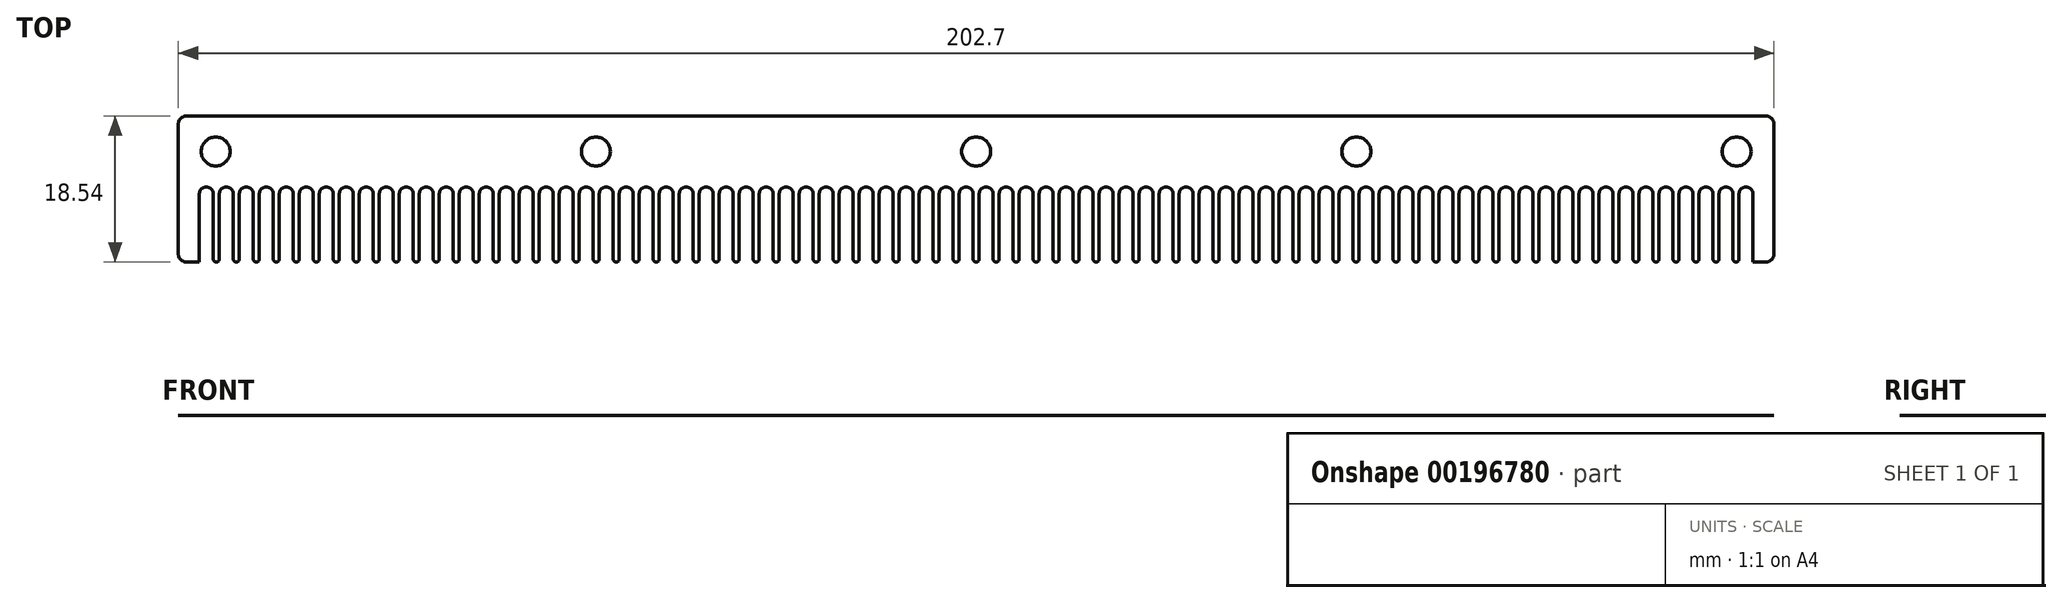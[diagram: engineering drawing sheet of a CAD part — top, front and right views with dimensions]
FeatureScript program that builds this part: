
annotation { "Feature Type Name" : "Feature", "Feature Type Description" : "" }
export const myFeature = defineFeature(function(context is Context, id is Id, definition is map)
    precondition{}
    {
        {
            var Q0;
            Q0=qCreatedBy(makeId("Top.planeOp"),FACE);
            var sketch = newSketch(context, id + "F0", { "sketchPlane" : qUnion([Q0])});
            skLineSegment(sketch, "E0.bottom", {"start": v(100.33, 9.52) * mm, "end": v(-100.33, 9.53) * mm});
            skLineSegment(sketch, "E0.left", {"start": v(101.6, 8.25) * mm, "end": v(101.6, -8.26) * mm});
            skLineSegment(sketch, "E0.right", {"start": v(-101.6, 8.26) * mm, "end": v(-101.6, -8.25) * mm});
            skPoint(sketch, "E0.middle", {"position": v(0, 0) * mm});
            skPoint(sketch, "E1.visualSharp", {"position": v(-101.6, 9.53) * mm});
            skArc(sketch, "E1.filletArc", {"start": v(-100.33, 9.53) * mm, "mid": v(-101.23, 9.15) * mm, "end": v(-101.6, 8.26) * mm});
            skPoint(sketch, "E2.visualSharp", {"position": v(-101.6, -9.52) * mm});
            skArc(sketch, "E2.filletArc", {"start": v(-101.6, -8.25) * mm, "mid": v(-101.23, -9.15) * mm, "end": v(-100.33, -9.52) * mm});
            skPoint(sketch, "E3.visualSharp", {"position": v(101.6, 9.52) * mm});
            skArc(sketch, "E3.filletArc", {"start": v(101.6, 8.25) * mm, "mid": v(101.23, 9.15) * mm, "end": v(100.33, 9.52) * mm});
            skPoint(sketch, "E4.visualSharp", {"position": v(101.6, -9.53) * mm});
            skArc(sketch, "E4.filletArc", {"start": v(100.33, -9.53) * mm, "mid": v(101.23, -9.15) * mm, "end": v(101.6, -8.26) * mm});
            skLineSegment(sketch, "E5", {"start": v(-98.42, -9.52) * mm, "end": v(-98.42, -0.63) * mm});
            skArc(sketch, "E6", {"start": v(-97.16, -0.63) * mm, "mid": v(-97.8, 0) * mm, "end": v(-98.43, -0.63) * mm});
            skLineSegment(sketch, "E7", {"start": v(-97.16, -0.63) * mm, "end": v(-97.16, -8.89) * mm});
            skArc(sketch, "E8", {"start": v(-97.16, -8.89) * mm, "mid": v(-96.52, -9.52) * mm, "end": v(-95.89, -8.89) * mm});
            skLineSegment(sketch, "E9", {"start": v(-95.89, -8.89) * mm, "end": v(-95.89, -0.63) * mm});
            skLineSegment(sketch, "E10.trimOffspring", {"start": v(-98.42, -9.52) * mm, "end": v(-100.33, -9.52) * mm});
            skArc(sketch, "E11.1.0.0", {"start": v(-94.62, -0.63) * mm, "mid": v(-95.25, 0) * mm, "end": v(-95.89, -0.63) * mm});
            skLineSegment(sketch, "E11.1.0.1", {"start": v(-94.62, -0.63) * mm, "end": v(-94.62, -8.89) * mm});
            skArc(sketch, "E11.1.0.2", {"start": v(-94.62, -8.89) * mm, "mid": v(-93.98, -9.52) * mm, "end": v(-93.35, -8.89) * mm});
            skLineSegment(sketch, "E11.1.0.3", {"start": v(-93.35, -8.89) * mm, "end": v(-93.35, -0.63) * mm});
            skArc(sketch, "E11.2.0.0", {"start": v(-92.08, -0.63) * mm, "mid": v(-92.71, 0) * mm, "end": v(-93.35, -0.63) * mm});
            skLineSegment(sketch, "E11.2.0.1", {"start": v(-92.08, -0.63) * mm, "end": v(-92.08, -8.89) * mm});
            skArc(sketch, "E11.2.0.2", {"start": v(-92.08, -8.89) * mm, "mid": v(-91.44, -9.52) * mm, "end": v(-90.8, -8.89) * mm});
            skLineSegment(sketch, "E11.2.0.3", {"start": v(-90.8, -8.89) * mm, "end": v(-90.8, -0.63) * mm});
            skArc(sketch, "E11.3.0.0", {"start": v(-89.54, -0.63) * mm, "mid": v(-90.17, 0) * mm, "end": v(-90.8, -0.63) * mm});
            skLineSegment(sketch, "E11.3.0.1", {"start": v(-89.54, -0.63) * mm, "end": v(-89.54, -8.89) * mm});
            skArc(sketch, "E11.3.0.2", {"start": v(-89.54, -8.89) * mm, "mid": v(-88.9, -9.52) * mm, "end": v(-88.27, -8.89) * mm});
            skLineSegment(sketch, "E11.3.0.3", {"start": v(-88.27, -8.89) * mm, "end": v(-88.27, -0.63) * mm});
            skArc(sketch, "E11.4.0.0", {"start": v(-87, -0.63) * mm, "mid": v(-87.63, 0) * mm, "end": v(-88.27, -0.63) * mm});
            skLineSegment(sketch, "E11.4.0.1", {"start": v(-87, -0.63) * mm, "end": v(-87, -8.89) * mm});
            skArc(sketch, "E11.4.0.2", {"start": v(-87, -8.89) * mm, "mid": v(-86.36, -9.52) * mm, "end": v(-85.73, -8.89) * mm});
            skLineSegment(sketch, "E11.4.0.3", {"start": v(-85.73, -8.89) * mm, "end": v(-85.73, -0.63) * mm});
            skArc(sketch, "E11.5.0.0", {"start": v(-84.46, -0.63) * mm, "mid": v(-85.1, 0) * mm, "end": v(-85.73, -0.63) * mm});
            skLineSegment(sketch, "E11.5.0.1", {"start": v(-84.46, -0.63) * mm, "end": v(-84.46, -8.89) * mm});
            skArc(sketch, "E11.5.0.2", {"start": v(-84.46, -8.89) * mm, "mid": v(-83.82, -9.52) * mm, "end": v(-83.19, -8.89) * mm});
            skLineSegment(sketch, "E11.5.0.3", {"start": v(-83.19, -8.89) * mm, "end": v(-83.19, -0.63) * mm});
            skArc(sketch, "E11.6.0.0", {"start": v(-81.92, -0.63) * mm, "mid": v(-82.55, 0) * mm, "end": v(-83.19, -0.63) * mm});
            skLineSegment(sketch, "E11.6.0.1", {"start": v(-81.92, -0.63) * mm, "end": v(-81.92, -8.89) * mm});
            skArc(sketch, "E11.6.0.2", {"start": v(-81.92, -8.89) * mm, "mid": v(-81.28, -9.52) * mm, "end": v(-80.65, -8.89) * mm});
            skLineSegment(sketch, "E11.6.0.3", {"start": v(-80.65, -8.89) * mm, "end": v(-80.65, -0.63) * mm});
            skArc(sketch, "E11.7.0.0", {"start": v(-79.38, -0.63) * mm, "mid": v(-80.01, 0) * mm, "end": v(-80.65, -0.63) * mm});
            skLineSegment(sketch, "E11.7.0.1", {"start": v(-79.38, -0.63) * mm, "end": v(-79.38, -8.89) * mm});
            skArc(sketch, "E11.7.0.2", {"start": v(-79.38, -8.89) * mm, "mid": v(-78.74, -9.52) * mm, "end": v(-78.1, -8.89) * mm});
            skLineSegment(sketch, "E11.7.0.3", {"start": v(-78.1, -8.89) * mm, "end": v(-78.1, -0.63) * mm});
            skArc(sketch, "E11.8.0.0", {"start": v(-76.84, -0.63) * mm, "mid": v(-77.47, 0) * mm, "end": v(-78.1, -0.63) * mm});
            skLineSegment(sketch, "E11.8.0.1", {"start": v(-76.84, -0.63) * mm, "end": v(-76.84, -8.89) * mm});
            skArc(sketch, "E11.8.0.2", {"start": v(-76.84, -8.89) * mm, "mid": v(-76.2, -9.52) * mm, "end": v(-75.57, -8.89) * mm});
            skLineSegment(sketch, "E11.8.0.3", {"start": v(-75.57, -8.89) * mm, "end": v(-75.57, -0.63) * mm});
            skArc(sketch, "E11.9.0.0", {"start": v(-74.3, -0.63) * mm, "mid": v(-74.93, 0) * mm, "end": v(-75.57, -0.63) * mm});
            skLineSegment(sketch, "E11.9.0.1", {"start": v(-74.3, -0.63) * mm, "end": v(-74.3, -8.89) * mm});
            skArc(sketch, "E11.9.0.2", {"start": v(-74.3, -8.89) * mm, "mid": v(-73.66, -9.52) * mm, "end": v(-73.03, -8.89) * mm});
            skLineSegment(sketch, "E11.9.0.3", {"start": v(-73.03, -8.89) * mm, "end": v(-73.03, -0.63) * mm});
            skArc(sketch, "E11.10.0.0", {"start": v(-71.76, -0.63) * mm, "mid": v(-72.4, 0) * mm, "end": v(-73.03, -0.63) * mm});
            skLineSegment(sketch, "E11.10.0.1", {"start": v(-71.76, -0.63) * mm, "end": v(-71.76, -8.89) * mm});
            skArc(sketch, "E11.10.0.2", {"start": v(-71.76, -8.89) * mm, "mid": v(-71.12, -9.52) * mm, "end": v(-70.49, -8.89) * mm});
            skLineSegment(sketch, "E11.10.0.3", {"start": v(-70.49, -8.89) * mm, "end": v(-70.49, -0.63) * mm});
            skArc(sketch, "E11.11.0.0", {"start": v(-69.22, -0.63) * mm, "mid": v(-69.85, 0) * mm, "end": v(-70.49, -0.63) * mm});
            skLineSegment(sketch, "E11.11.0.1", {"start": v(-69.22, -0.63) * mm, "end": v(-69.22, -8.89) * mm});
            skArc(sketch, "E11.11.0.2", {"start": v(-69.22, -8.89) * mm, "mid": v(-68.58, -9.52) * mm, "end": v(-67.95, -8.89) * mm});
            skLineSegment(sketch, "E11.11.0.3", {"start": v(-67.95, -8.89) * mm, "end": v(-67.95, -0.63) * mm});
            skArc(sketch, "E11.12.0.0", {"start": v(-66.68, -0.63) * mm, "mid": v(-67.31, 0) * mm, "end": v(-67.95, -0.63) * mm});
            skLineSegment(sketch, "E11.12.0.1", {"start": v(-66.68, -0.63) * mm, "end": v(-66.68, -8.89) * mm});
            skArc(sketch, "E11.12.0.2", {"start": v(-66.68, -8.89) * mm, "mid": v(-66.04, -9.52) * mm, "end": v(-65.4, -8.89) * mm});
            skLineSegment(sketch, "E11.12.0.3", {"start": v(-65.4, -8.89) * mm, "end": v(-65.4, -0.63) * mm});
            skArc(sketch, "E11.13.0.0", {"start": v(-64.14, -0.63) * mm, "mid": v(-64.77, 0) * mm, "end": v(-65.4, -0.63) * mm});
            skLineSegment(sketch, "E11.13.0.1", {"start": v(-64.14, -0.63) * mm, "end": v(-64.14, -8.89) * mm});
            skArc(sketch, "E11.13.0.2", {"start": v(-64.14, -8.89) * mm, "mid": v(-63.5, -9.52) * mm, "end": v(-62.87, -8.89) * mm});
            skLineSegment(sketch, "E11.13.0.3", {"start": v(-62.87, -8.89) * mm, "end": v(-62.87, -0.63) * mm});
            skArc(sketch, "E11.14.0.0", {"start": v(-61.6, -0.63) * mm, "mid": v(-62.23, 0) * mm, "end": v(-62.87, -0.63) * mm});
            skLineSegment(sketch, "E11.14.0.1", {"start": v(-61.6, -0.63) * mm, "end": v(-61.6, -8.89) * mm});
            skArc(sketch, "E11.14.0.2", {"start": v(-61.6, -8.89) * mm, "mid": v(-60.96, -9.52) * mm, "end": v(-60.33, -8.89) * mm});
            skLineSegment(sketch, "E11.14.0.3", {"start": v(-60.33, -8.89) * mm, "end": v(-60.33, -0.63) * mm});
            skArc(sketch, "E11.15.0.0", {"start": v(-59.06, -0.63) * mm, "mid": v(-59.7, 0) * mm, "end": v(-60.33, -0.63) * mm});
            skLineSegment(sketch, "E11.15.0.1", {"start": v(-59.06, -0.63) * mm, "end": v(-59.06, -8.89) * mm});
            skArc(sketch, "E11.15.0.2", {"start": v(-59.06, -8.89) * mm, "mid": v(-58.42, -9.52) * mm, "end": v(-57.79, -8.89) * mm});
            skLineSegment(sketch, "E11.15.0.3", {"start": v(-57.79, -8.89) * mm, "end": v(-57.79, -0.63) * mm});
            skArc(sketch, "E11.16.0.0", {"start": v(-56.52, -0.63) * mm, "mid": v(-57.15, 0) * mm, "end": v(-57.79, -0.63) * mm});
            skLineSegment(sketch, "E11.16.0.1", {"start": v(-56.52, -0.63) * mm, "end": v(-56.52, -8.89) * mm});
            skArc(sketch, "E11.16.0.2", {"start": v(-56.52, -8.89) * mm, "mid": v(-55.88, -9.52) * mm, "end": v(-55.25, -8.89) * mm});
            skLineSegment(sketch, "E11.16.0.3", {"start": v(-55.25, -8.89) * mm, "end": v(-55.25, -0.63) * mm});
            skArc(sketch, "E11.17.0.0", {"start": v(-53.98, -0.63) * mm, "mid": v(-54.61, 0) * mm, "end": v(-55.25, -0.63) * mm});
            skLineSegment(sketch, "E11.17.0.1", {"start": v(-53.98, -0.63) * mm, "end": v(-53.98, -8.89) * mm});
            skArc(sketch, "E11.17.0.2", {"start": v(-53.98, -8.89) * mm, "mid": v(-53.34, -9.52) * mm, "end": v(-52.7, -8.89) * mm});
            skLineSegment(sketch, "E11.17.0.3", {"start": v(-52.7, -8.89) * mm, "end": v(-52.7, -0.63) * mm});
            skArc(sketch, "E11.18.0.0", {"start": v(-51.44, -0.63) * mm, "mid": v(-52.07, 0) * mm, "end": v(-52.7, -0.63) * mm});
            skLineSegment(sketch, "E11.18.0.1", {"start": v(-51.44, -0.63) * mm, "end": v(-51.44, -8.89) * mm});
            skArc(sketch, "E11.18.0.2", {"start": v(-51.44, -8.89) * mm, "mid": v(-50.8, -9.52) * mm, "end": v(-50.17, -8.89) * mm});
            skLineSegment(sketch, "E11.18.0.3", {"start": v(-50.17, -8.89) * mm, "end": v(-50.17, -0.63) * mm});
            skArc(sketch, "E11.19.0.0", {"start": v(-48.9, -0.63) * mm, "mid": v(-49.53, 0) * mm, "end": v(-50.17, -0.63) * mm});
            skLineSegment(sketch, "E11.19.0.1", {"start": v(-48.9, -0.63) * mm, "end": v(-48.9, -8.89) * mm});
            skArc(sketch, "E11.19.0.2", {"start": v(-48.9, -8.89) * mm, "mid": v(-48.26, -9.52) * mm, "end": v(-47.63, -8.89) * mm});
            skLineSegment(sketch, "E11.19.0.3", {"start": v(-47.63, -8.89) * mm, "end": v(-47.63, -0.63) * mm});
            skArc(sketch, "E11.20.0.0", {"start": v(-46.36, -0.63) * mm, "mid": v(-47, 0) * mm, "end": v(-47.63, -0.63) * mm});
            skLineSegment(sketch, "E11.20.0.1", {"start": v(-46.36, -0.63) * mm, "end": v(-46.36, -8.89) * mm});
            skArc(sketch, "E11.20.0.2", {"start": v(-46.36, -8.89) * mm, "mid": v(-45.72, -9.52) * mm, "end": v(-45.09, -8.89) * mm});
            skLineSegment(sketch, "E11.20.0.3", {"start": v(-45.09, -8.89) * mm, "end": v(-45.09, -0.63) * mm});
            skArc(sketch, "E11.21.0.0", {"start": v(-43.82, -0.63) * mm, "mid": v(-44.45, 0) * mm, "end": v(-45.09, -0.63) * mm});
            skLineSegment(sketch, "E11.21.0.1", {"start": v(-43.82, -0.63) * mm, "end": v(-43.82, -8.89) * mm});
            skArc(sketch, "E11.21.0.2", {"start": v(-43.82, -8.89) * mm, "mid": v(-43.18, -9.52) * mm, "end": v(-42.55, -8.89) * mm});
            skLineSegment(sketch, "E11.21.0.3", {"start": v(-42.55, -8.89) * mm, "end": v(-42.55, -0.63) * mm});
            skArc(sketch, "E11.22.0.0", {"start": v(-41.28, -0.63) * mm, "mid": v(-41.91, 0) * mm, "end": v(-42.55, -0.63) * mm});
            skLineSegment(sketch, "E11.22.0.1", {"start": v(-41.28, -0.63) * mm, "end": v(-41.28, -8.89) * mm});
            skArc(sketch, "E11.22.0.2", {"start": v(-41.28, -8.89) * mm, "mid": v(-40.64, -9.52) * mm, "end": v(-40, -8.89) * mm});
            skLineSegment(sketch, "E11.22.0.3", {"start": v(-40, -8.89) * mm, "end": v(-40, -0.63) * mm});
            skArc(sketch, "E11.23.0.0", {"start": v(-38.74, -0.63) * mm, "mid": v(-39.37, 0) * mm, "end": v(-40, -0.63) * mm});
            skLineSegment(sketch, "E11.23.0.1", {"start": v(-38.74, -0.63) * mm, "end": v(-38.74, -8.89) * mm});
            skArc(sketch, "E11.23.0.2", {"start": v(-38.74, -8.89) * mm, "mid": v(-38.1, -9.52) * mm, "end": v(-37.47, -8.89) * mm});
            skLineSegment(sketch, "E11.23.0.3", {"start": v(-37.47, -8.89) * mm, "end": v(-37.47, -0.63) * mm});
            skArc(sketch, "E11.24.0.0", {"start": v(-36.2, -0.63) * mm, "mid": v(-36.83, 0) * mm, "end": v(-37.47, -0.63) * mm});
            skLineSegment(sketch, "E11.24.0.1", {"start": v(-36.2, -0.63) * mm, "end": v(-36.2, -8.89) * mm});
            skArc(sketch, "E11.24.0.2", {"start": v(-36.2, -8.89) * mm, "mid": v(-35.56, -9.52) * mm, "end": v(-34.93, -8.89) * mm});
            skLineSegment(sketch, "E11.24.0.3", {"start": v(-34.93, -8.89) * mm, "end": v(-34.93, -0.63) * mm});
            skArc(sketch, "E11.25.0.0", {"start": v(-33.66, -0.63) * mm, "mid": v(-34.3, 0) * mm, "end": v(-34.93, -0.63) * mm});
            skLineSegment(sketch, "E11.25.0.1", {"start": v(-33.66, -0.63) * mm, "end": v(-33.66, -8.89) * mm});
            skArc(sketch, "E11.25.0.2", {"start": v(-33.66, -8.89) * mm, "mid": v(-33.02, -9.52) * mm, "end": v(-32.39, -8.89) * mm});
            skLineSegment(sketch, "E11.25.0.3", {"start": v(-32.39, -8.89) * mm, "end": v(-32.39, -0.63) * mm});
            skArc(sketch, "E11.26.0.0", {"start": v(-31.12, -0.63) * mm, "mid": v(-31.75, 0) * mm, "end": v(-32.39, -0.63) * mm});
            skLineSegment(sketch, "E11.26.0.1", {"start": v(-31.12, -0.63) * mm, "end": v(-31.12, -8.89) * mm});
            skArc(sketch, "E11.26.0.2", {"start": v(-31.12, -8.89) * mm, "mid": v(-30.48, -9.52) * mm, "end": v(-29.85, -8.89) * mm});
            skLineSegment(sketch, "E11.26.0.3", {"start": v(-29.85, -8.89) * mm, "end": v(-29.85, -0.63) * mm});
            skArc(sketch, "E11.27.0.0", {"start": v(-28.58, -0.63) * mm, "mid": v(-29.21, 0) * mm, "end": v(-29.85, -0.63) * mm});
            skLineSegment(sketch, "E11.27.0.1", {"start": v(-28.58, -0.63) * mm, "end": v(-28.58, -8.89) * mm});
            skArc(sketch, "E11.27.0.2", {"start": v(-28.58, -8.89) * mm, "mid": v(-27.94, -9.52) * mm, "end": v(-27.3, -8.89) * mm});
            skLineSegment(sketch, "E11.27.0.3", {"start": v(-27.3, -8.89) * mm, "end": v(-27.3, -0.63) * mm});
            skArc(sketch, "E11.28.0.0", {"start": v(-26.04, -0.63) * mm, "mid": v(-26.67, 0) * mm, "end": v(-27.3, -0.63) * mm});
            skLineSegment(sketch, "E11.28.0.1", {"start": v(-26.04, -0.63) * mm, "end": v(-26.04, -8.89) * mm});
            skArc(sketch, "E11.28.0.2", {"start": v(-26.04, -8.89) * mm, "mid": v(-25.4, -9.52) * mm, "end": v(-24.77, -8.89) * mm});
            skLineSegment(sketch, "E11.28.0.3", {"start": v(-24.77, -8.89) * mm, "end": v(-24.77, -0.63) * mm});
            skArc(sketch, "E11.29.0.0", {"start": v(-23.5, -0.63) * mm, "mid": v(-24.13, 0) * mm, "end": v(-24.77, -0.63) * mm});
            skLineSegment(sketch, "E11.29.0.1", {"start": v(-23.5, -0.63) * mm, "end": v(-23.5, -8.89) * mm});
            skArc(sketch, "E11.29.0.2", {"start": v(-23.5, -8.89) * mm, "mid": v(-22.86, -9.52) * mm, "end": v(-22.23, -8.89) * mm});
            skLineSegment(sketch, "E11.29.0.3", {"start": v(-22.23, -8.89) * mm, "end": v(-22.23, -0.63) * mm});
            skArc(sketch, "E11.30.0.0", {"start": v(-20.96, -0.63) * mm, "mid": v(-21.6, 0) * mm, "end": v(-22.23, -0.63) * mm});
            skLineSegment(sketch, "E11.30.0.1", {"start": v(-20.96, -0.63) * mm, "end": v(-20.96, -8.89) * mm});
            skArc(sketch, "E11.30.0.2", {"start": v(-20.96, -8.89) * mm, "mid": v(-20.32, -9.52) * mm, "end": v(-19.69, -8.89) * mm});
            skLineSegment(sketch, "E11.30.0.3", {"start": v(-19.69, -8.89) * mm, "end": v(-19.69, -0.63) * mm});
            skArc(sketch, "E11.31.0.0", {"start": v(-18.42, -0.63) * mm, "mid": v(-19.05, 0) * mm, "end": v(-19.69, -0.63) * mm});
            skLineSegment(sketch, "E11.31.0.1", {"start": v(-18.41, -0.63) * mm, "end": v(-18.41, -8.89) * mm});
            skArc(sketch, "E11.31.0.2", {"start": v(-18.41, -8.89) * mm, "mid": v(-17.78, -9.52) * mm, "end": v(-17.15, -8.89) * mm});
            skLineSegment(sketch, "E11.31.0.3", {"start": v(-17.15, -8.89) * mm, "end": v(-17.15, -0.63) * mm});
            skArc(sketch, "E11.32.0.0", {"start": v(-15.88, -0.63) * mm, "mid": v(-16.51, 0) * mm, "end": v(-17.15, -0.63) * mm});
            skLineSegment(sketch, "E11.32.0.1", {"start": v(-15.88, -0.63) * mm, "end": v(-15.88, -8.89) * mm});
            skArc(sketch, "E11.32.0.2", {"start": v(-15.88, -8.89) * mm, "mid": v(-15.24, -9.52) * mm, "end": v(-14.6, -8.89) * mm});
            skLineSegment(sketch, "E11.32.0.3", {"start": v(-14.6, -8.89) * mm, "end": v(-14.6, -0.63) * mm});
            skArc(sketch, "E11.33.0.0", {"start": v(-13.34, -0.63) * mm, "mid": v(-13.97, 0) * mm, "end": v(-14.6, -0.63) * mm});
            skLineSegment(sketch, "E11.33.0.1", {"start": v(-13.33, -0.63) * mm, "end": v(-13.33, -8.89) * mm});
            skArc(sketch, "E11.33.0.2", {"start": v(-13.33, -8.89) * mm, "mid": v(-12.7, -9.52) * mm, "end": v(-12.07, -8.89) * mm});
            skLineSegment(sketch, "E11.33.0.3", {"start": v(-12.07, -8.89) * mm, "end": v(-12.07, -0.63) * mm});
            skArc(sketch, "E11.34.0.0", {"start": v(-10.8, -0.63) * mm, "mid": v(-11.43, 0) * mm, "end": v(-12.07, -0.63) * mm});
            skLineSegment(sketch, "E11.34.0.1", {"start": v(-10.8, -0.63) * mm, "end": v(-10.8, -8.89) * mm});
            skArc(sketch, "E11.34.0.2", {"start": v(-10.8, -8.89) * mm, "mid": v(-10.16, -9.52) * mm, "end": v(-9.53, -8.89) * mm});
            skLineSegment(sketch, "E11.34.0.3", {"start": v(-9.53, -8.89) * mm, "end": v(-9.53, -0.63) * mm});
            skArc(sketch, "E11.35.0.0", {"start": v(-8.26, -0.63) * mm, "mid": v(-8.9, 0) * mm, "end": v(-9.53, -0.63) * mm});
            skLineSegment(sketch, "E11.35.0.1", {"start": v(-8.25, -0.63) * mm, "end": v(-8.25, -8.89) * mm});
            skArc(sketch, "E11.35.0.2", {"start": v(-8.25, -8.89) * mm, "mid": v(-7.62, -9.52) * mm, "end": v(-6.99, -8.89) * mm});
            skLineSegment(sketch, "E11.35.0.3", {"start": v(-6.99, -8.89) * mm, "end": v(-6.99, -0.63) * mm});
            skArc(sketch, "E11.36.0.0", {"start": v(-5.72, -0.63) * mm, "mid": v(-6.35, 0) * mm, "end": v(-6.99, -0.63) * mm});
            skLineSegment(sketch, "E11.36.0.1", {"start": v(-5.71, -0.63) * mm, "end": v(-5.71, -8.89) * mm});
            skArc(sketch, "E11.36.0.2", {"start": v(-5.71, -8.89) * mm, "mid": v(-5.08, -9.52) * mm, "end": v(-4.45, -8.89) * mm});
            skLineSegment(sketch, "E11.36.0.3", {"start": v(-4.45, -8.89) * mm, "end": v(-4.45, -0.63) * mm});
            skArc(sketch, "E11.37.0.0", {"start": v(-3.18, -0.63) * mm, "mid": v(-3.81, 0) * mm, "end": v(-4.45, -0.63) * mm});
            skLineSegment(sketch, "E11.37.0.1", {"start": v(-3.17, -0.63) * mm, "end": v(-3.17, -8.89) * mm});
            skArc(sketch, "E11.37.0.2", {"start": v(-3.17, -8.89) * mm, "mid": v(-2.54, -9.52) * mm, "end": v(-1.9, -8.89) * mm});
            skLineSegment(sketch, "E11.37.0.3", {"start": v(-1.9, -8.89) * mm, "end": v(-1.9, -0.63) * mm});
            skArc(sketch, "E11.38.0.0", {"start": v(-0.64, -0.63) * mm, "mid": v(-1.27, 0) * mm, "end": v(-1.9, -0.63) * mm});
            skLineSegment(sketch, "E11.38.0.1", {"start": v(-0.63, -0.63) * mm, "end": v(-0.63, -8.89) * mm});
            skArc(sketch, "E11.38.0.2", {"start": v(-0.63, -8.89) * mm, "mid": v(0, -9.52) * mm, "end": v(0.63, -8.89) * mm});
            skLineSegment(sketch, "E11.38.0.3", {"start": v(0.63, -8.89) * mm, "end": v(0.63, -0.63) * mm});
            skArc(sketch, "E11.39.0.0", {"start": v(1.9, -0.63) * mm, "mid": v(1.27, 0) * mm, "end": v(0.63, -0.63) * mm});
            skLineSegment(sketch, "E11.39.0.1", {"start": v(1.9, -0.63) * mm, "end": v(1.9, -8.89) * mm});
            skArc(sketch, "E11.39.0.2", {"start": v(1.9, -8.89) * mm, "mid": v(2.54, -9.52) * mm, "end": v(3.17, -8.89) * mm});
            skLineSegment(sketch, "E11.39.0.3", {"start": v(3.17, -8.89) * mm, "end": v(3.17, -0.63) * mm});
            skArc(sketch, "E11.40.0.0", {"start": v(4.44, -0.63) * mm, "mid": v(3.8, 0) * mm, "end": v(3.17, -0.63) * mm});
            skLineSegment(sketch, "E11.40.0.1", {"start": v(4.45, -0.63) * mm, "end": v(4.45, -8.89) * mm});
            skArc(sketch, "E11.40.0.2", {"start": v(4.45, -8.89) * mm, "mid": v(5.08, -9.52) * mm, "end": v(5.71, -8.89) * mm});
            skLineSegment(sketch, "E11.40.0.3", {"start": v(5.71, -8.89) * mm, "end": v(5.71, -0.63) * mm});
            skArc(sketch, "E11.41.0.0", {"start": v(6.98, -0.63) * mm, "mid": v(6.35, 0) * mm, "end": v(5.71, -0.63) * mm});
            skLineSegment(sketch, "E11.41.0.1", {"start": v(6.99, -0.63) * mm, "end": v(6.99, -8.89) * mm});
            skArc(sketch, "E11.41.0.2", {"start": v(6.99, -8.89) * mm, "mid": v(7.62, -9.52) * mm, "end": v(8.25, -8.89) * mm});
            skLineSegment(sketch, "E11.41.0.3", {"start": v(8.25, -8.89) * mm, "end": v(8.25, -0.63) * mm});
            skArc(sketch, "E11.42.0.0", {"start": v(9.52, -0.63) * mm, "mid": v(8.9, 0) * mm, "end": v(8.25, -0.63) * mm});
            skLineSegment(sketch, "E11.42.0.1", {"start": v(9.53, -0.63) * mm, "end": v(9.53, -8.89) * mm});
            skArc(sketch, "E11.42.0.2", {"start": v(9.53, -8.89) * mm, "mid": v(10.16, -9.52) * mm, "end": v(10.8, -8.89) * mm});
            skLineSegment(sketch, "E11.42.0.3", {"start": v(10.8, -8.89) * mm, "end": v(10.8, -0.63) * mm});
            skArc(sketch, "E11.43.0.0", {"start": v(12.06, -0.63) * mm, "mid": v(11.43, 0) * mm, "end": v(10.8, -0.63) * mm});
            skLineSegment(sketch, "E11.43.0.1", {"start": v(12.07, -0.63) * mm, "end": v(12.07, -8.89) * mm});
            skArc(sketch, "E11.43.0.2", {"start": v(12.07, -8.89) * mm, "mid": v(12.7, -9.52) * mm, "end": v(13.33, -8.89) * mm});
            skLineSegment(sketch, "E11.43.0.3", {"start": v(13.33, -8.89) * mm, "end": v(13.33, -0.63) * mm});
            skArc(sketch, "E11.44.0.0", {"start": v(14.6, -0.63) * mm, "mid": v(13.97, 0) * mm, "end": v(13.33, -0.63) * mm});
            skLineSegment(sketch, "E11.44.0.1", {"start": v(14.6, -0.63) * mm, "end": v(14.6, -8.89) * mm});
            skArc(sketch, "E11.44.0.2", {"start": v(14.6, -8.89) * mm, "mid": v(15.24, -9.52) * mm, "end": v(15.88, -8.89) * mm});
            skLineSegment(sketch, "E11.44.0.3", {"start": v(15.88, -8.89) * mm, "end": v(15.88, -0.63) * mm});
            skArc(sketch, "E11.45.0.0", {"start": v(17.14, -0.63) * mm, "mid": v(16.51, 0) * mm, "end": v(15.88, -0.63) * mm});
            skLineSegment(sketch, "E11.45.0.1", {"start": v(17.15, -0.63) * mm, "end": v(17.15, -8.89) * mm});
            skArc(sketch, "E11.45.0.2", {"start": v(17.15, -8.89) * mm, "mid": v(17.78, -9.52) * mm, "end": v(18.41, -8.89) * mm});
            skLineSegment(sketch, "E11.45.0.3", {"start": v(18.41, -8.89) * mm, "end": v(18.41, -0.63) * mm});
            skArc(sketch, "E11.46.0.0", {"start": v(19.68, -0.63) * mm, "mid": v(19.05, 0) * mm, "end": v(18.41, -0.63) * mm});
            skLineSegment(sketch, "E11.46.0.1", {"start": v(19.69, -0.63) * mm, "end": v(19.69, -8.89) * mm});
            skArc(sketch, "E11.46.0.2", {"start": v(19.69, -8.89) * mm, "mid": v(20.32, -9.52) * mm, "end": v(20.96, -8.89) * mm});
            skLineSegment(sketch, "E11.46.0.3", {"start": v(20.96, -8.89) * mm, "end": v(20.96, -0.63) * mm});
            skArc(sketch, "E11.47.0.0", {"start": v(22.22, -0.63) * mm, "mid": v(21.59, 0) * mm, "end": v(20.96, -0.63) * mm});
            skLineSegment(sketch, "E11.47.0.1", {"start": v(22.23, -0.63) * mm, "end": v(22.23, -8.89) * mm});
            skArc(sketch, "E11.47.0.2", {"start": v(22.23, -8.89) * mm, "mid": v(22.86, -9.52) * mm, "end": v(23.5, -8.89) * mm});
            skLineSegment(sketch, "E11.47.0.3", {"start": v(23.5, -8.89) * mm, "end": v(23.5, -0.63) * mm});
            skArc(sketch, "E11.48.0.0", {"start": v(24.76, -0.63) * mm, "mid": v(24.13, 0) * mm, "end": v(23.5, -0.63) * mm});
            skLineSegment(sketch, "E11.48.0.1", {"start": v(24.77, -0.63) * mm, "end": v(24.77, -8.89) * mm});
            skArc(sketch, "E11.48.0.2", {"start": v(24.77, -8.89) * mm, "mid": v(25.4, -9.52) * mm, "end": v(26.04, -8.89) * mm});
            skLineSegment(sketch, "E11.48.0.3", {"start": v(26.04, -8.89) * mm, "end": v(26.04, -0.63) * mm});
            skArc(sketch, "E11.49.0.0", {"start": v(27.3, -0.63) * mm, "mid": v(26.67, 0) * mm, "end": v(26.04, -0.63) * mm});
            skLineSegment(sketch, "E11.49.0.1", {"start": v(27.3, -0.63) * mm, "end": v(27.3, -8.89) * mm});
            skArc(sketch, "E11.49.0.2", {"start": v(27.3, -8.89) * mm, "mid": v(27.94, -9.52) * mm, "end": v(28.58, -8.89) * mm});
            skLineSegment(sketch, "E11.49.0.3", {"start": v(28.58, -8.89) * mm, "end": v(28.58, -0.63) * mm});
            skArc(sketch, "E11.50.0.0", {"start": v(29.84, -0.63) * mm, "mid": v(29.21, 0) * mm, "end": v(28.58, -0.63) * mm});
            skLineSegment(sketch, "E11.50.0.1", {"start": v(29.85, -0.63) * mm, "end": v(29.85, -8.89) * mm});
            skArc(sketch, "E11.50.0.2", {"start": v(29.85, -8.89) * mm, "mid": v(30.48, -9.52) * mm, "end": v(31.12, -8.89) * mm});
            skLineSegment(sketch, "E11.50.0.3", {"start": v(31.12, -8.89) * mm, "end": v(31.12, -0.63) * mm});
            skArc(sketch, "E11.51.0.0", {"start": v(32.39, -0.63) * mm, "mid": v(31.75, 0) * mm, "end": v(31.12, -0.63) * mm});
            skLineSegment(sketch, "E11.51.0.1", {"start": v(32.39, -0.63) * mm, "end": v(32.39, -8.89) * mm});
            skArc(sketch, "E11.51.0.2", {"start": v(32.39, -8.89) * mm, "mid": v(33.02, -9.52) * mm, "end": v(33.66, -8.89) * mm});
            skLineSegment(sketch, "E11.51.0.3", {"start": v(33.66, -8.89) * mm, "end": v(33.66, -0.63) * mm});
            skArc(sketch, "E11.52.0.0", {"start": v(34.92, -0.63) * mm, "mid": v(34.3, 0) * mm, "end": v(33.66, -0.63) * mm});
            skLineSegment(sketch, "E11.52.0.1", {"start": v(34.93, -0.63) * mm, "end": v(34.93, -8.89) * mm});
            skArc(sketch, "E11.52.0.2", {"start": v(34.93, -8.89) * mm, "mid": v(35.56, -9.52) * mm, "end": v(36.2, -8.89) * mm});
            skLineSegment(sketch, "E11.52.0.3", {"start": v(36.2, -8.89) * mm, "end": v(36.2, -0.63) * mm});
            skArc(sketch, "E11.53.0.0", {"start": v(37.46, -0.63) * mm, "mid": v(36.83, 0) * mm, "end": v(36.2, -0.63) * mm});
            skLineSegment(sketch, "E11.53.0.1", {"start": v(37.46, -0.63) * mm, "end": v(37.46, -8.89) * mm});
            skArc(sketch, "E11.53.0.2", {"start": v(37.46, -8.89) * mm, "mid": v(38.1, -9.52) * mm, "end": v(38.73, -8.89) * mm});
            skLineSegment(sketch, "E11.53.0.3", {"start": v(38.73, -8.89) * mm, "end": v(38.73, -0.63) * mm});
            skArc(sketch, "E11.54.0.0", {"start": v(40, -0.63) * mm, "mid": v(39.37, 0) * mm, "end": v(38.74, -0.63) * mm});
            skLineSegment(sketch, "E11.54.0.1", {"start": v(40, -0.63) * mm, "end": v(40, -8.89) * mm});
            skArc(sketch, "E11.54.0.2", {"start": v(40, -8.89) * mm, "mid": v(40.64, -9.52) * mm, "end": v(41.28, -8.89) * mm});
            skLineSegment(sketch, "E11.54.0.3", {"start": v(41.28, -8.89) * mm, "end": v(41.28, -0.63) * mm});
            skArc(sketch, "E11.55.0.0", {"start": v(42.55, -0.63) * mm, "mid": v(41.91, 0) * mm, "end": v(41.28, -0.63) * mm});
            skLineSegment(sketch, "E11.55.0.1", {"start": v(42.55, -0.63) * mm, "end": v(42.55, -8.89) * mm});
            skArc(sketch, "E11.55.0.2", {"start": v(42.55, -8.89) * mm, "mid": v(43.18, -9.52) * mm, "end": v(43.82, -8.89) * mm});
            skLineSegment(sketch, "E11.55.0.3", {"start": v(43.82, -8.89) * mm, "end": v(43.82, -0.63) * mm});
            skArc(sketch, "E11.56.0.0", {"start": v(45.09, -0.63) * mm, "mid": v(44.45, 0) * mm, "end": v(43.82, -0.63) * mm});
            skLineSegment(sketch, "E11.56.0.1", {"start": v(45.09, -0.63) * mm, "end": v(45.09, -8.89) * mm});
            skArc(sketch, "E11.56.0.2", {"start": v(45.09, -8.89) * mm, "mid": v(45.72, -9.52) * mm, "end": v(46.36, -8.89) * mm});
            skLineSegment(sketch, "E11.56.0.3", {"start": v(46.36, -8.89) * mm, "end": v(46.36, -0.63) * mm});
            skArc(sketch, "E11.57.0.0", {"start": v(47.62, -0.63) * mm, "mid": v(46.99, 0) * mm, "end": v(46.35, -0.63) * mm});
            skLineSegment(sketch, "E11.57.0.1", {"start": v(47.62, -0.63) * mm, "end": v(47.62, -8.89) * mm});
            skArc(sketch, "E11.57.0.2", {"start": v(47.62, -8.89) * mm, "mid": v(48.26, -9.52) * mm, "end": v(48.9, -8.89) * mm});
            skLineSegment(sketch, "E11.57.0.3", {"start": v(48.9, -8.89) * mm, "end": v(48.9, -0.63) * mm});
            skArc(sketch, "E11.58.0.0", {"start": v(50.16, -0.63) * mm, "mid": v(49.53, 0) * mm, "end": v(48.9, -0.63) * mm});
            skLineSegment(sketch, "E11.58.0.1", {"start": v(50.17, -0.63) * mm, "end": v(50.17, -8.89) * mm});
            skArc(sketch, "E11.58.0.2", {"start": v(50.17, -8.89) * mm, "mid": v(50.8, -9.52) * mm, "end": v(51.44, -8.89) * mm});
            skLineSegment(sketch, "E11.58.0.3", {"start": v(51.44, -8.89) * mm, "end": v(51.44, -0.63) * mm});
            skArc(sketch, "E11.59.0.0", {"start": v(52.7, -0.63) * mm, "mid": v(52.07, 0) * mm, "end": v(51.44, -0.63) * mm});
            skLineSegment(sketch, "E11.59.0.1", {"start": v(52.7, -0.63) * mm, "end": v(52.7, -8.89) * mm});
            skArc(sketch, "E11.59.0.2", {"start": v(52.7, -8.89) * mm, "mid": v(53.34, -9.52) * mm, "end": v(53.98, -8.89) * mm});
            skLineSegment(sketch, "E11.59.0.3", {"start": v(53.98, -8.89) * mm, "end": v(53.98, -0.63) * mm});
            skArc(sketch, "E11.60.0.0", {"start": v(55.25, -0.63) * mm, "mid": v(54.61, 0) * mm, "end": v(53.98, -0.63) * mm});
            skLineSegment(sketch, "E11.60.0.1", {"start": v(55.25, -0.63) * mm, "end": v(55.25, -8.89) * mm});
            skArc(sketch, "E11.60.0.2", {"start": v(55.25, -8.89) * mm, "mid": v(55.88, -9.52) * mm, "end": v(56.52, -8.89) * mm});
            skLineSegment(sketch, "E11.60.0.3", {"start": v(56.52, -8.89) * mm, "end": v(56.52, -0.63) * mm});
            skArc(sketch, "E11.61.0.0", {"start": v(57.78, -0.63) * mm, "mid": v(57.15, 0) * mm, "end": v(56.51, -0.63) * mm});
            skLineSegment(sketch, "E11.61.0.1", {"start": v(57.79, -0.63) * mm, "end": v(57.79, -8.89) * mm});
            skArc(sketch, "E11.61.0.2", {"start": v(57.79, -8.89) * mm, "mid": v(58.42, -9.52) * mm, "end": v(59.05, -8.89) * mm});
            skLineSegment(sketch, "E11.61.0.3", {"start": v(59.05, -8.89) * mm, "end": v(59.05, -0.63) * mm});
            skArc(sketch, "E11.62.0.0", {"start": v(60.33, -0.63) * mm, "mid": v(59.7, 0) * mm, "end": v(59.06, -0.63) * mm});
            skLineSegment(sketch, "E11.62.0.1", {"start": v(60.33, -0.63) * mm, "end": v(60.33, -8.89) * mm});
            skArc(sketch, "E11.62.0.2", {"start": v(60.33, -8.89) * mm, "mid": v(60.96, -9.52) * mm, "end": v(61.6, -8.89) * mm});
            skLineSegment(sketch, "E11.62.0.3", {"start": v(61.6, -8.89) * mm, "end": v(61.6, -0.63) * mm});
            skArc(sketch, "E11.63.0.0", {"start": v(62.87, -0.63) * mm, "mid": v(62.23, 0) * mm, "end": v(61.6, -0.63) * mm});
            skLineSegment(sketch, "E11.63.0.1", {"start": v(62.87, -0.63) * mm, "end": v(62.87, -8.89) * mm});
            skArc(sketch, "E11.63.0.2", {"start": v(62.87, -8.89) * mm, "mid": v(63.5, -9.52) * mm, "end": v(64.14, -8.89) * mm});
            skLineSegment(sketch, "E11.63.0.3", {"start": v(64.14, -8.89) * mm, "end": v(64.14, -0.63) * mm});
            skArc(sketch, "E11.64.0.0", {"start": v(65.4, -0.63) * mm, "mid": v(64.77, 0) * mm, "end": v(64.14, -0.63) * mm});
            skLineSegment(sketch, "E11.64.0.1", {"start": v(65.4, -0.63) * mm, "end": v(65.4, -8.89) * mm});
            skArc(sketch, "E11.64.0.2", {"start": v(65.4, -8.89) * mm, "mid": v(66.04, -9.52) * mm, "end": v(66.68, -8.89) * mm});
            skLineSegment(sketch, "E11.64.0.3", {"start": v(66.68, -8.89) * mm, "end": v(66.68, -0.63) * mm});
            skArc(sketch, "E11.65.0.0", {"start": v(67.94, -0.63) * mm, "mid": v(67.3, 0) * mm, "end": v(66.67, -0.63) * mm});
            skLineSegment(sketch, "E11.65.0.1", {"start": v(67.95, -0.63) * mm, "end": v(67.95, -8.89) * mm});
            skArc(sketch, "E11.65.0.2", {"start": v(67.95, -8.89) * mm, "mid": v(68.58, -9.52) * mm, "end": v(69.22, -8.89) * mm});
            skLineSegment(sketch, "E11.65.0.3", {"start": v(69.22, -8.89) * mm, "end": v(69.22, -0.63) * mm});
            skArc(sketch, "E11.66.0.0", {"start": v(70.48, -0.63) * mm, "mid": v(69.85, 0) * mm, "end": v(69.22, -0.63) * mm});
            skLineSegment(sketch, "E11.66.0.1", {"start": v(70.49, -0.63) * mm, "end": v(70.49, -8.89) * mm});
            skArc(sketch, "E11.66.0.2", {"start": v(70.49, -8.89) * mm, "mid": v(71.12, -9.52) * mm, "end": v(71.76, -8.89) * mm});
            skLineSegment(sketch, "E11.66.0.3", {"start": v(71.76, -8.89) * mm, "end": v(71.76, -0.63) * mm});
            skArc(sketch, "E11.67.0.0", {"start": v(73.03, -0.63) * mm, "mid": v(72.4, 0) * mm, "end": v(71.76, -0.63) * mm});
            skLineSegment(sketch, "E11.67.0.1", {"start": v(73.03, -0.63) * mm, "end": v(73.03, -8.89) * mm});
            skArc(sketch, "E11.67.0.2", {"start": v(73.03, -8.89) * mm, "mid": v(73.66, -9.52) * mm, "end": v(74.3, -8.89) * mm});
            skLineSegment(sketch, "E11.67.0.3", {"start": v(74.3, -8.89) * mm, "end": v(74.3, -0.63) * mm});
            skArc(sketch, "E11.68.0.0", {"start": v(75.57, -0.63) * mm, "mid": v(74.93, 0) * mm, "end": v(74.3, -0.63) * mm});
            skLineSegment(sketch, "E11.68.0.1", {"start": v(75.57, -0.63) * mm, "end": v(75.57, -8.89) * mm});
            skArc(sketch, "E11.68.0.2", {"start": v(75.57, -8.89) * mm, "mid": v(76.2, -9.52) * mm, "end": v(76.84, -8.89) * mm});
            skLineSegment(sketch, "E11.68.0.3", {"start": v(76.84, -8.89) * mm, "end": v(76.84, -0.63) * mm});
            skArc(sketch, "E11.69.0.0", {"start": v(78.1, -0.63) * mm, "mid": v(77.47, 0) * mm, "end": v(76.83, -0.63) * mm});
            skLineSegment(sketch, "E11.69.0.1", {"start": v(78.1, -0.63) * mm, "end": v(78.1, -8.89) * mm});
            skArc(sketch, "E11.69.0.2", {"start": v(78.1, -8.89) * mm, "mid": v(78.74, -9.52) * mm, "end": v(79.38, -8.89) * mm});
            skLineSegment(sketch, "E11.69.0.3", {"start": v(79.38, -8.89) * mm, "end": v(79.38, -0.63) * mm});
            skArc(sketch, "E11.70.0.0", {"start": v(80.65, -0.63) * mm, "mid": v(80.01, 0) * mm, "end": v(79.38, -0.63) * mm});
            skLineSegment(sketch, "E11.70.0.1", {"start": v(80.65, -0.63) * mm, "end": v(80.65, -8.89) * mm});
            skArc(sketch, "E11.70.0.2", {"start": v(80.65, -8.89) * mm, "mid": v(81.28, -9.52) * mm, "end": v(81.92, -8.89) * mm});
            skLineSegment(sketch, "E11.70.0.3", {"start": v(81.92, -8.89) * mm, "end": v(81.92, -0.63) * mm});
            skArc(sketch, "E11.71.0.0", {"start": v(83.19, -0.63) * mm, "mid": v(82.55, 0) * mm, "end": v(81.92, -0.63) * mm});
            skLineSegment(sketch, "E11.71.0.1", {"start": v(83.19, -0.63) * mm, "end": v(83.19, -8.89) * mm});
            skArc(sketch, "E11.71.0.2", {"start": v(83.19, -8.89) * mm, "mid": v(83.82, -9.52) * mm, "end": v(84.46, -8.89) * mm});
            skLineSegment(sketch, "E11.71.0.3", {"start": v(84.46, -8.89) * mm, "end": v(84.46, -0.63) * mm});
            skArc(sketch, "E11.72.0.0", {"start": v(85.73, -0.63) * mm, "mid": v(85.1, 0) * mm, "end": v(84.46, -0.63) * mm});
            skLineSegment(sketch, "E11.72.0.1", {"start": v(85.73, -0.63) * mm, "end": v(85.73, -8.89) * mm});
            skArc(sketch, "E11.72.0.2", {"start": v(85.73, -8.89) * mm, "mid": v(86.36, -9.52) * mm, "end": v(87, -8.89) * mm});
            skLineSegment(sketch, "E11.72.0.3", {"start": v(87, -8.89) * mm, "end": v(87, -0.63) * mm});
            skArc(sketch, "E11.73.0.0", {"start": v(88.27, -0.63) * mm, "mid": v(87.63, 0) * mm, "end": v(87, -0.63) * mm});
            skLineSegment(sketch, "E11.73.0.1", {"start": v(88.27, -0.63) * mm, "end": v(88.27, -8.89) * mm});
            skArc(sketch, "E11.73.0.2", {"start": v(88.27, -8.89) * mm, "mid": v(88.9, -9.52) * mm, "end": v(89.53, -8.89) * mm});
            skLineSegment(sketch, "E11.73.0.3", {"start": v(89.53, -8.89) * mm, "end": v(89.53, -0.63) * mm});
            skArc(sketch, "E11.74.0.0", {"start": v(90.8, -0.63) * mm, "mid": v(90.17, 0) * mm, "end": v(89.54, -0.63) * mm});
            skLineSegment(sketch, "E11.74.0.1", {"start": v(90.8, -0.63) * mm, "end": v(90.8, -8.89) * mm});
            skArc(sketch, "E11.74.0.2", {"start": v(90.8, -8.89) * mm, "mid": v(91.44, -9.52) * mm, "end": v(92.08, -8.89) * mm});
            skLineSegment(sketch, "E11.74.0.3", {"start": v(92.08, -8.89) * mm, "end": v(92.08, -0.63) * mm});
            skArc(sketch, "E11.75.0.0", {"start": v(93.35, -0.63) * mm, "mid": v(92.71, 0) * mm, "end": v(92.08, -0.63) * mm});
            skLineSegment(sketch, "E11.75.0.1", {"start": v(93.35, -0.63) * mm, "end": v(93.35, -8.89) * mm});
            skArc(sketch, "E11.75.0.2", {"start": v(93.35, -8.89) * mm, "mid": v(93.98, -9.52) * mm, "end": v(94.62, -8.89) * mm});
            skLineSegment(sketch, "E11.75.0.3", {"start": v(94.62, -8.89) * mm, "end": v(94.62, -0.63) * mm});
            skArc(sketch, "E11.76.0.0", {"start": v(95.89, -0.63) * mm, "mid": v(95.25, 0) * mm, "end": v(94.62, -0.63) * mm});
            skLineSegment(sketch, "E11.76.0.1", {"start": v(95.89, -0.63) * mm, "end": v(95.89, -8.89) * mm});
            skArc(sketch, "E11.76.0.2", {"start": v(95.89, -8.89) * mm, "mid": v(96.52, -9.52) * mm, "end": v(97.16, -8.89) * mm});
            skLineSegment(sketch, "E11.76.0.3", {"start": v(97.16, -8.89) * mm, "end": v(97.16, -0.63) * mm});
            skLineSegment(sketch, "E11.direction1", {"start": v(-98.43, -0.63) * mm, "end": v(-95.89, -0.63) * mm, "construction": true});
            skArc(sketch, "E12", {"start": v(98.42, -0.64) * mm, "mid": v(97.79, 0) * mm, "end": v(97.15, -0.63) * mm});
            skLineSegment(sketch, "E13", {"start": v(98.42, -0.64) * mm, "end": v(98.42, -9.53) * mm});
            skLineSegment(sketch, "E14", {"start": v(98.42, -9.53) * mm, "end": v(100.33, -9.53) * mm});
            skPoint(sketch, "E15.end.orphan", {"position": v(-98.49, 4.76) * mm});
            skCircle(sketch, "E16", {"center": v(-96.6, 4.76) * mm, "radius": 1.59 * mm});
            skPoint(sketch, "E17.orphan", {"position": v(-101.6, 4.76) * mm});
            skPoint(sketch, "E18.end.orphan", {"position": v(92.73, 4.76) * mm});
            skCircle(sketch, "E19", {"center": v(96.6, 4.76) * mm, "radius": 1.59 * mm});
            skPoint(sketch, "E20.start.orphan", {"position": v(101.6, 4.76) * mm});
            skCircle(sketch, "E21", {"center": v(0, 4.76) * mm, "radius": 1.59 * mm});
            skCircle(sketch, "E22", {"center": v(48.3, 4.76) * mm, "radius": 1.59 * mm});
            skCircle(sketch, "E23", {"center": v(-48.3, 4.76) * mm, "radius": 1.59 * mm});
            skSolve(sketch);
        }
        {
            var Q0;
            Q0=makeQuery(id+"F0.imprint","IMPRINT",FACE,{"disambiguationData":[TD([[makeQuery(id+"F0.imprint","IMPRINT",EDGE,{"derivedFrom":sQuery(id+"F0.wireOp",EDGE,"E0.bottom")}),1.0]])]});
            extrude(context, id + "F1", {"entities" : qUnion([Q0]), "depth" : 1 / 406.4 * mm});
        }
        {
            var Q0;
            Q0=makeQuery(id+"F1.opExtrude","CAP_FACE",FACE,{"disambiguationData":[OSD([sQuery(id+"F0.wireOp",EDGE,"E0.bottom"),sQuery(id+"F0.wireOp",EDGE,"E0.left"),sQuery(id+"F0.wireOp",EDGE,"E0.right"),sQuery(id+"F0.wireOp",EDGE,"E1.filletArc"),sQuery(id+"F0.wireOp",EDGE,"E2.filletArc"),sQuery(id+"F0.wireOp",EDGE,"E3.filletArc"),sQuery(id+"F0.wireOp",EDGE,"E4.filletArc"),sQuery(id+"F0.wireOp",EDGE,"E5"),sQuery(id+"F0.wireOp",EDGE,"E6"),sQuery(id+"F0.wireOp",EDGE,"E7"),sQuery(id+"F0.wireOp",EDGE,"E8"),sQuery(id+"F0.wireOp",EDGE,"E9"),sQuery(id+"F0.wireOp",EDGE,"E10.trimOffspring"),sQuery(id+"F0.wireOp",EDGE,"E11.1.0.0"),sQuery(id+"F0.wireOp",EDGE,"E11.1.0.1"),sQuery(id+"F0.wireOp",EDGE,"E11.1.0.2"),sQuery(id+"F0.wireOp",EDGE,"E11.1.0.3"),sQuery(id+"F0.wireOp",EDGE,"E11.2.0.0"),sQuery(id+"F0.wireOp",EDGE,"E11.2.0.1"),sQuery(id+"F0.wireOp",EDGE,"E11.2.0.2"),sQuery(id+"F0.wireOp",EDGE,"E11.2.0.3"),sQuery(id+"F0.wireOp",EDGE,"E11.3.0.0"),sQuery(id+"F0.wireOp",EDGE,"E11.3.0.1"),sQuery(id+"F0.wireOp",EDGE,"E11.3.0.2"),sQuery(id+"F0.wireOp",EDGE,"E11.3.0.3"),sQuery(id+"F0.wireOp",EDGE,"E11.4.0.0"),sQuery(id+"F0.wireOp",EDGE,"E11.4.0.1"),sQuery(id+"F0.wireOp",EDGE,"E11.4.0.2"),sQuery(id+"F0.wireOp",EDGE,"E11.4.0.3"),sQuery(id+"F0.wireOp",EDGE,"E11.5.0.0"),sQuery(id+"F0.wireOp",EDGE,"E11.5.0.1"),sQuery(id+"F0.wireOp",EDGE,"E11.5.0.2"),sQuery(id+"F0.wireOp",EDGE,"E11.5.0.3"),sQuery(id+"F0.wireOp",EDGE,"E11.6.0.0"),sQuery(id+"F0.wireOp",EDGE,"E11.6.0.1"),sQuery(id+"F0.wireOp",EDGE,"E11.6.0.2"),sQuery(id+"F0.wireOp",EDGE,"E11.6.0.3"),sQuery(id+"F0.wireOp",EDGE,"E11.7.0.0"),sQuery(id+"F0.wireOp",EDGE,"E11.7.0.1"),sQuery(id+"F0.wireOp",EDGE,"E11.7.0.2"),sQuery(id+"F0.wireOp",EDGE,"E11.7.0.3"),sQuery(id+"F0.wireOp",EDGE,"E11.8.0.0"),sQuery(id+"F0.wireOp",EDGE,"E11.8.0.1"),sQuery(id+"F0.wireOp",EDGE,"E11.8.0.2"),sQuery(id+"F0.wireOp",EDGE,"E11.8.0.3"),sQuery(id+"F0.wireOp",EDGE,"E11.9.0.0"),sQuery(id+"F0.wireOp",EDGE,"E11.9.0.1"),sQuery(id+"F0.wireOp",EDGE,"E11.9.0.2"),sQuery(id+"F0.wireOp",EDGE,"E11.9.0.3"),sQuery(id+"F0.wireOp",EDGE,"E11.10.0.0"),sQuery(id+"F0.wireOp",EDGE,"E11.10.0.1"),sQuery(id+"F0.wireOp",EDGE,"E11.10.0.2"),sQuery(id+"F0.wireOp",EDGE,"E11.10.0.3"),sQuery(id+"F0.wireOp",EDGE,"E11.11.0.0"),sQuery(id+"F0.wireOp",EDGE,"E11.11.0.1"),sQuery(id+"F0.wireOp",EDGE,"E11.11.0.2"),sQuery(id+"F0.wireOp",EDGE,"E11.11.0.3"),sQuery(id+"F0.wireOp",EDGE,"E11.12.0.0"),sQuery(id+"F0.wireOp",EDGE,"E11.12.0.1"),sQuery(id+"F0.wireOp",EDGE,"E11.12.0.2"),sQuery(id+"F0.wireOp",EDGE,"E11.12.0.3"),sQuery(id+"F0.wireOp",EDGE,"E11.13.0.0"),sQuery(id+"F0.wireOp",EDGE,"E11.13.0.1"),sQuery(id+"F0.wireOp",EDGE,"E11.13.0.2"),sQuery(id+"F0.wireOp",EDGE,"E11.13.0.3"),sQuery(id+"F0.wireOp",EDGE,"E11.14.0.0"),sQuery(id+"F0.wireOp",EDGE,"E11.14.0.1"),sQuery(id+"F0.wireOp",EDGE,"E11.14.0.2"),sQuery(id+"F0.wireOp",EDGE,"E11.14.0.3"),sQuery(id+"F0.wireOp",EDGE,"E11.15.0.0"),sQuery(id+"F0.wireOp",EDGE,"E11.15.0.1"),sQuery(id+"F0.wireOp",EDGE,"E11.15.0.2"),sQuery(id+"F0.wireOp",EDGE,"E11.15.0.3"),sQuery(id+"F0.wireOp",EDGE,"E11.16.0.0"),sQuery(id+"F0.wireOp",EDGE,"E11.16.0.1"),sQuery(id+"F0.wireOp",EDGE,"E11.16.0.2"),sQuery(id+"F0.wireOp",EDGE,"E11.16.0.3"),sQuery(id+"F0.wireOp",EDGE,"E11.17.0.0"),sQuery(id+"F0.wireOp",EDGE,"E11.17.0.1"),sQuery(id+"F0.wireOp",EDGE,"E11.17.0.2"),sQuery(id+"F0.wireOp",EDGE,"E11.17.0.3"),sQuery(id+"F0.wireOp",EDGE,"E11.18.0.0"),sQuery(id+"F0.wireOp",EDGE,"E11.18.0.1"),sQuery(id+"F0.wireOp",EDGE,"E11.18.0.2"),sQuery(id+"F0.wireOp",EDGE,"E11.18.0.3"),sQuery(id+"F0.wireOp",EDGE,"E11.19.0.0"),sQuery(id+"F0.wireOp",EDGE,"E11.19.0.1"),sQuery(id+"F0.wireOp",EDGE,"E11.19.0.2"),sQuery(id+"F0.wireOp",EDGE,"E11.19.0.3"),sQuery(id+"F0.wireOp",EDGE,"E11.20.0.0"),sQuery(id+"F0.wireOp",EDGE,"E11.20.0.1"),sQuery(id+"F0.wireOp",EDGE,"E11.20.0.2"),sQuery(id+"F0.wireOp",EDGE,"E11.20.0.3"),sQuery(id+"F0.wireOp",EDGE,"E11.21.0.0"),sQuery(id+"F0.wireOp",EDGE,"E11.21.0.1"),sQuery(id+"F0.wireOp",EDGE,"E11.21.0.2"),sQuery(id+"F0.wireOp",EDGE,"E11.21.0.3"),sQuery(id+"F0.wireOp",EDGE,"E11.22.0.0"),sQuery(id+"F0.wireOp",EDGE,"E11.22.0.1"),sQuery(id+"F0.wireOp",EDGE,"E11.22.0.2"),sQuery(id+"F0.wireOp",EDGE,"E11.22.0.3"),sQuery(id+"F0.wireOp",EDGE,"E11.23.0.0"),sQuery(id+"F0.wireOp",EDGE,"E11.23.0.1"),sQuery(id+"F0.wireOp",EDGE,"E11.23.0.2"),sQuery(id+"F0.wireOp",EDGE,"E11.23.0.3"),sQuery(id+"F0.wireOp",EDGE,"E11.24.0.0"),sQuery(id+"F0.wireOp",EDGE,"E11.24.0.1"),sQuery(id+"F0.wireOp",EDGE,"E11.24.0.2"),sQuery(id+"F0.wireOp",EDGE,"E11.24.0.3"),sQuery(id+"F0.wireOp",EDGE,"E11.25.0.0"),sQuery(id+"F0.wireOp",EDGE,"E11.25.0.1"),sQuery(id+"F0.wireOp",EDGE,"E11.25.0.2"),sQuery(id+"F0.wireOp",EDGE,"E11.25.0.3"),sQuery(id+"F0.wireOp",EDGE,"E11.26.0.0"),sQuery(id+"F0.wireOp",EDGE,"E11.26.0.1"),sQuery(id+"F0.wireOp",EDGE,"E11.26.0.2"),sQuery(id+"F0.wireOp",EDGE,"E11.26.0.3"),sQuery(id+"F0.wireOp",EDGE,"E11.27.0.0"),sQuery(id+"F0.wireOp",EDGE,"E11.27.0.1"),sQuery(id+"F0.wireOp",EDGE,"E11.27.0.2"),sQuery(id+"F0.wireOp",EDGE,"E11.27.0.3"),sQuery(id+"F0.wireOp",EDGE,"E11.28.0.0"),sQuery(id+"F0.wireOp",EDGE,"E11.28.0.1"),sQuery(id+"F0.wireOp",EDGE,"E11.28.0.2"),sQuery(id+"F0.wireOp",EDGE,"E11.28.0.3"),sQuery(id+"F0.wireOp",EDGE,"E11.29.0.0"),sQuery(id+"F0.wireOp",EDGE,"E11.29.0.1"),sQuery(id+"F0.wireOp",EDGE,"E11.29.0.2"),sQuery(id+"F0.wireOp",EDGE,"E11.29.0.3"),sQuery(id+"F0.wireOp",EDGE,"E11.30.0.0"),sQuery(id+"F0.wireOp",EDGE,"E11.30.0.1"),sQuery(id+"F0.wireOp",EDGE,"E11.30.0.2"),sQuery(id+"F0.wireOp",EDGE,"E11.30.0.3"),sQuery(id+"F0.wireOp",EDGE,"E11.31.0.0"),sQuery(id+"F0.wireOp",EDGE,"E11.31.0.1"),sQuery(id+"F0.wireOp",EDGE,"E11.31.0.2"),sQuery(id+"F0.wireOp",EDGE,"E11.31.0.3"),sQuery(id+"F0.wireOp",EDGE,"E11.32.0.0"),sQuery(id+"F0.wireOp",EDGE,"E11.32.0.1"),sQuery(id+"F0.wireOp",EDGE,"E11.32.0.2"),sQuery(id+"F0.wireOp",EDGE,"E11.32.0.3"),sQuery(id+"F0.wireOp",EDGE,"E11.33.0.0"),sQuery(id+"F0.wireOp",EDGE,"E11.33.0.1"),sQuery(id+"F0.wireOp",EDGE,"E11.33.0.2"),sQuery(id+"F0.wireOp",EDGE,"E11.33.0.3"),sQuery(id+"F0.wireOp",EDGE,"E11.34.0.0"),sQuery(id+"F0.wireOp",EDGE,"E11.34.0.1"),sQuery(id+"F0.wireOp",EDGE,"E11.34.0.2"),sQuery(id+"F0.wireOp",EDGE,"E11.34.0.3"),sQuery(id+"F0.wireOp",EDGE,"E11.35.0.0"),sQuery(id+"F0.wireOp",EDGE,"E11.35.0.1"),sQuery(id+"F0.wireOp",EDGE,"E11.35.0.2"),sQuery(id+"F0.wireOp",EDGE,"E11.35.0.3"),sQuery(id+"F0.wireOp",EDGE,"E11.36.0.0"),sQuery(id+"F0.wireOp",EDGE,"E11.36.0.1"),sQuery(id+"F0.wireOp",EDGE,"E11.36.0.2"),sQuery(id+"F0.wireOp",EDGE,"E11.36.0.3"),sQuery(id+"F0.wireOp",EDGE,"E11.37.0.0"),sQuery(id+"F0.wireOp",EDGE,"E11.37.0.1"),sQuery(id+"F0.wireOp",EDGE,"E11.37.0.2"),sQuery(id+"F0.wireOp",EDGE,"E11.37.0.3"),sQuery(id+"F0.wireOp",EDGE,"E11.38.0.0"),sQuery(id+"F0.wireOp",EDGE,"E11.38.0.1"),sQuery(id+"F0.wireOp",EDGE,"E11.38.0.2"),sQuery(id+"F0.wireOp",EDGE,"E11.38.0.3"),sQuery(id+"F0.wireOp",EDGE,"E11.39.0.0"),sQuery(id+"F0.wireOp",EDGE,"E11.39.0.1"),sQuery(id+"F0.wireOp",EDGE,"E11.39.0.2"),sQuery(id+"F0.wireOp",EDGE,"E11.39.0.3"),sQuery(id+"F0.wireOp",EDGE,"E11.40.0.0"),sQuery(id+"F0.wireOp",EDGE,"E11.40.0.1"),sQuery(id+"F0.wireOp",EDGE,"E11.40.0.2"),sQuery(id+"F0.wireOp",EDGE,"E11.40.0.3"),sQuery(id+"F0.wireOp",EDGE,"E11.41.0.0"),sQuery(id+"F0.wireOp",EDGE,"E11.41.0.1"),sQuery(id+"F0.wireOp",EDGE,"E11.41.0.2"),sQuery(id+"F0.wireOp",EDGE,"E11.41.0.3"),sQuery(id+"F0.wireOp",EDGE,"E11.42.0.0"),sQuery(id+"F0.wireOp",EDGE,"E11.42.0.1"),sQuery(id+"F0.wireOp",EDGE,"E11.42.0.2"),sQuery(id+"F0.wireOp",EDGE,"E11.42.0.3"),sQuery(id+"F0.wireOp",EDGE,"E11.43.0.0"),sQuery(id+"F0.wireOp",EDGE,"E11.43.0.1"),sQuery(id+"F0.wireOp",EDGE,"E11.43.0.2"),sQuery(id+"F0.wireOp",EDGE,"E11.43.0.3"),sQuery(id+"F0.wireOp",EDGE,"E11.44.0.0"),sQuery(id+"F0.wireOp",EDGE,"E11.44.0.1"),sQuery(id+"F0.wireOp",EDGE,"E11.44.0.2"),sQuery(id+"F0.wireOp",EDGE,"E11.44.0.3"),sQuery(id+"F0.wireOp",EDGE,"E11.45.0.0"),sQuery(id+"F0.wireOp",EDGE,"E11.45.0.1"),sQuery(id+"F0.wireOp",EDGE,"E11.45.0.2"),sQuery(id+"F0.wireOp",EDGE,"E11.45.0.3"),sQuery(id+"F0.wireOp",EDGE,"E11.46.0.0"),sQuery(id+"F0.wireOp",EDGE,"E11.46.0.1"),sQuery(id+"F0.wireOp",EDGE,"E11.46.0.2"),sQuery(id+"F0.wireOp",EDGE,"E11.46.0.3"),sQuery(id+"F0.wireOp",EDGE,"E11.47.0.0"),sQuery(id+"F0.wireOp",EDGE,"E11.47.0.1"),sQuery(id+"F0.wireOp",EDGE,"E11.47.0.2"),sQuery(id+"F0.wireOp",EDGE,"E11.47.0.3"),sQuery(id+"F0.wireOp",EDGE,"E11.48.0.0"),sQuery(id+"F0.wireOp",EDGE,"E11.48.0.1"),sQuery(id+"F0.wireOp",EDGE,"E11.48.0.2"),sQuery(id+"F0.wireOp",EDGE,"E11.48.0.3"),sQuery(id+"F0.wireOp",EDGE,"E11.49.0.0"),sQuery(id+"F0.wireOp",EDGE,"E11.49.0.1"),sQuery(id+"F0.wireOp",EDGE,"E11.49.0.2"),sQuery(id+"F0.wireOp",EDGE,"E11.49.0.3"),sQuery(id+"F0.wireOp",EDGE,"E11.50.0.0"),sQuery(id+"F0.wireOp",EDGE,"E11.50.0.1"),sQuery(id+"F0.wireOp",EDGE,"E11.50.0.2"),sQuery(id+"F0.wireOp",EDGE,"E11.50.0.3"),sQuery(id+"F0.wireOp",EDGE,"E11.51.0.0"),sQuery(id+"F0.wireOp",EDGE,"E11.51.0.1"),sQuery(id+"F0.wireOp",EDGE,"E11.51.0.2"),sQuery(id+"F0.wireOp",EDGE,"E11.51.0.3"),sQuery(id+"F0.wireOp",EDGE,"E11.52.0.0"),sQuery(id+"F0.wireOp",EDGE,"E11.52.0.1"),sQuery(id+"F0.wireOp",EDGE,"E11.52.0.2"),sQuery(id+"F0.wireOp",EDGE,"E11.52.0.3"),sQuery(id+"F0.wireOp",EDGE,"E11.53.0.0"),sQuery(id+"F0.wireOp",EDGE,"E11.53.0.1"),sQuery(id+"F0.wireOp",EDGE,"E11.53.0.2"),sQuery(id+"F0.wireOp",EDGE,"E11.53.0.3"),sQuery(id+"F0.wireOp",EDGE,"E11.54.0.0"),sQuery(id+"F0.wireOp",EDGE,"E11.54.0.1"),sQuery(id+"F0.wireOp",EDGE,"E11.54.0.2"),sQuery(id+"F0.wireOp",EDGE,"E11.54.0.3"),sQuery(id+"F0.wireOp",EDGE,"E11.55.0.0"),sQuery(id+"F0.wireOp",EDGE,"E11.55.0.1"),sQuery(id+"F0.wireOp",EDGE,"E11.55.0.2"),sQuery(id+"F0.wireOp",EDGE,"E11.55.0.3"),sQuery(id+"F0.wireOp",EDGE,"E11.56.0.0"),sQuery(id+"F0.wireOp",EDGE,"E11.56.0.1"),sQuery(id+"F0.wireOp",EDGE,"E11.56.0.2"),sQuery(id+"F0.wireOp",EDGE,"E11.56.0.3"),sQuery(id+"F0.wireOp",EDGE,"E11.57.0.0"),sQuery(id+"F0.wireOp",EDGE,"E11.57.0.1"),sQuery(id+"F0.wireOp",EDGE,"E11.57.0.2"),sQuery(id+"F0.wireOp",EDGE,"E11.57.0.3"),sQuery(id+"F0.wireOp",EDGE,"E11.58.0.0"),sQuery(id+"F0.wireOp",EDGE,"E11.58.0.1"),sQuery(id+"F0.wireOp",EDGE,"E11.58.0.2"),sQuery(id+"F0.wireOp",EDGE,"E11.58.0.3"),sQuery(id+"F0.wireOp",EDGE,"E11.59.0.0"),sQuery(id+"F0.wireOp",EDGE,"E11.59.0.1"),sQuery(id+"F0.wireOp",EDGE,"E11.59.0.2"),sQuery(id+"F0.wireOp",EDGE,"E11.59.0.3"),sQuery(id+"F0.wireOp",EDGE,"E11.60.0.0"),sQuery(id+"F0.wireOp",EDGE,"E11.60.0.1"),sQuery(id+"F0.wireOp",EDGE,"E11.60.0.2"),sQuery(id+"F0.wireOp",EDGE,"E11.60.0.3"),sQuery(id+"F0.wireOp",EDGE,"E11.61.0.0"),sQuery(id+"F0.wireOp",EDGE,"E11.61.0.1"),sQuery(id+"F0.wireOp",EDGE,"E11.61.0.2"),sQuery(id+"F0.wireOp",EDGE,"E11.61.0.3"),sQuery(id+"F0.wireOp",EDGE,"E11.62.0.0"),sQuery(id+"F0.wireOp",EDGE,"E11.62.0.1"),sQuery(id+"F0.wireOp",EDGE,"E11.62.0.2"),sQuery(id+"F0.wireOp",EDGE,"E11.62.0.3"),sQuery(id+"F0.wireOp",EDGE,"E11.63.0.0"),sQuery(id+"F0.wireOp",EDGE,"E11.63.0.1"),sQuery(id+"F0.wireOp",EDGE,"E11.63.0.2"),sQuery(id+"F0.wireOp",EDGE,"E11.63.0.3"),sQuery(id+"F0.wireOp",EDGE,"E11.64.0.0"),sQuery(id+"F0.wireOp",EDGE,"E11.64.0.1"),sQuery(id+"F0.wireOp",EDGE,"E11.64.0.2"),sQuery(id+"F0.wireOp",EDGE,"E11.64.0.3"),sQuery(id+"F0.wireOp",EDGE,"E11.65.0.0"),sQuery(id+"F0.wireOp",EDGE,"E11.65.0.1"),sQuery(id+"F0.wireOp",EDGE,"E11.65.0.2"),sQuery(id+"F0.wireOp",EDGE,"E11.65.0.3"),sQuery(id+"F0.wireOp",EDGE,"E11.66.0.0"),sQuery(id+"F0.wireOp",EDGE,"E11.66.0.1"),sQuery(id+"F0.wireOp",EDGE,"E11.66.0.2"),sQuery(id+"F0.wireOp",EDGE,"E11.66.0.3"),sQuery(id+"F0.wireOp",EDGE,"E11.67.0.0"),sQuery(id+"F0.wireOp",EDGE,"E11.67.0.1"),sQuery(id+"F0.wireOp",EDGE,"E11.67.0.2"),sQuery(id+"F0.wireOp",EDGE,"E11.67.0.3"),sQuery(id+"F0.wireOp",EDGE,"E11.68.0.0"),sQuery(id+"F0.wireOp",EDGE,"E11.68.0.1"),sQuery(id+"F0.wireOp",EDGE,"E11.68.0.2"),sQuery(id+"F0.wireOp",EDGE,"E11.68.0.3"),sQuery(id+"F0.wireOp",EDGE,"E11.69.0.0"),sQuery(id+"F0.wireOp",EDGE,"E11.69.0.1"),sQuery(id+"F0.wireOp",EDGE,"E11.69.0.2"),sQuery(id+"F0.wireOp",EDGE,"E11.69.0.3"),sQuery(id+"F0.wireOp",EDGE,"E11.70.0.0"),sQuery(id+"F0.wireOp",EDGE,"E11.70.0.1"),sQuery(id+"F0.wireOp",EDGE,"E11.70.0.2"),sQuery(id+"F0.wireOp",EDGE,"E11.70.0.3"),sQuery(id+"F0.wireOp",EDGE,"E11.71.0.0"),sQuery(id+"F0.wireOp",EDGE,"E11.71.0.1"),sQuery(id+"F0.wireOp",EDGE,"E11.71.0.2"),sQuery(id+"F0.wireOp",EDGE,"E11.71.0.3"),sQuery(id+"F0.wireOp",EDGE,"E11.72.0.0"),sQuery(id+"F0.wireOp",EDGE,"E11.72.0.1"),sQuery(id+"F0.wireOp",EDGE,"E11.72.0.2"),sQuery(id+"F0.wireOp",EDGE,"E11.72.0.3"),sQuery(id+"F0.wireOp",EDGE,"E11.73.0.0"),sQuery(id+"F0.wireOp",EDGE,"E11.73.0.1"),sQuery(id+"F0.wireOp",EDGE,"E11.73.0.2"),sQuery(id+"F0.wireOp",EDGE,"E11.73.0.3"),sQuery(id+"F0.wireOp",EDGE,"E11.74.0.0"),sQuery(id+"F0.wireOp",EDGE,"E11.74.0.1"),sQuery(id+"F0.wireOp",EDGE,"E11.74.0.2"),sQuery(id+"F0.wireOp",EDGE,"E11.74.0.3"),sQuery(id+"F0.wireOp",EDGE,"E11.75.0.0"),sQuery(id+"F0.wireOp",EDGE,"E11.75.0.1"),sQuery(id+"F0.wireOp",EDGE,"E11.75.0.2"),sQuery(id+"F0.wireOp",EDGE,"E11.75.0.3"),sQuery(id+"F0.wireOp",EDGE,"E11.76.0.0"),sQuery(id+"F0.wireOp",EDGE,"E11.76.0.1"),sQuery(id+"F0.wireOp",EDGE,"E11.76.0.2"),sQuery(id+"F0.wireOp",EDGE,"E11.76.0.3"),sQuery(id+"F0.wireOp",EDGE,"E12"),sQuery(id+"F0.wireOp",EDGE,"E13"),sQuery(id+"F0.wireOp",EDGE,"E14"),sQuery(id+"F0.wireOp",EDGE,"E16"),sQuery(id+"F0.wireOp",EDGE,"E19"),sQuery(id+"F0.wireOp",EDGE,"E21"),sQuery(id+"F0.wireOp",EDGE,"E22"),sQuery(id+"F0.wireOp",EDGE,"E23")])],"isStart":false});
            chamfer(context, id + "F2", {"entities" : qUnion([Q0]), "width" : 0.25 * mm, "tangentPropagation" : true});
        }
    });
